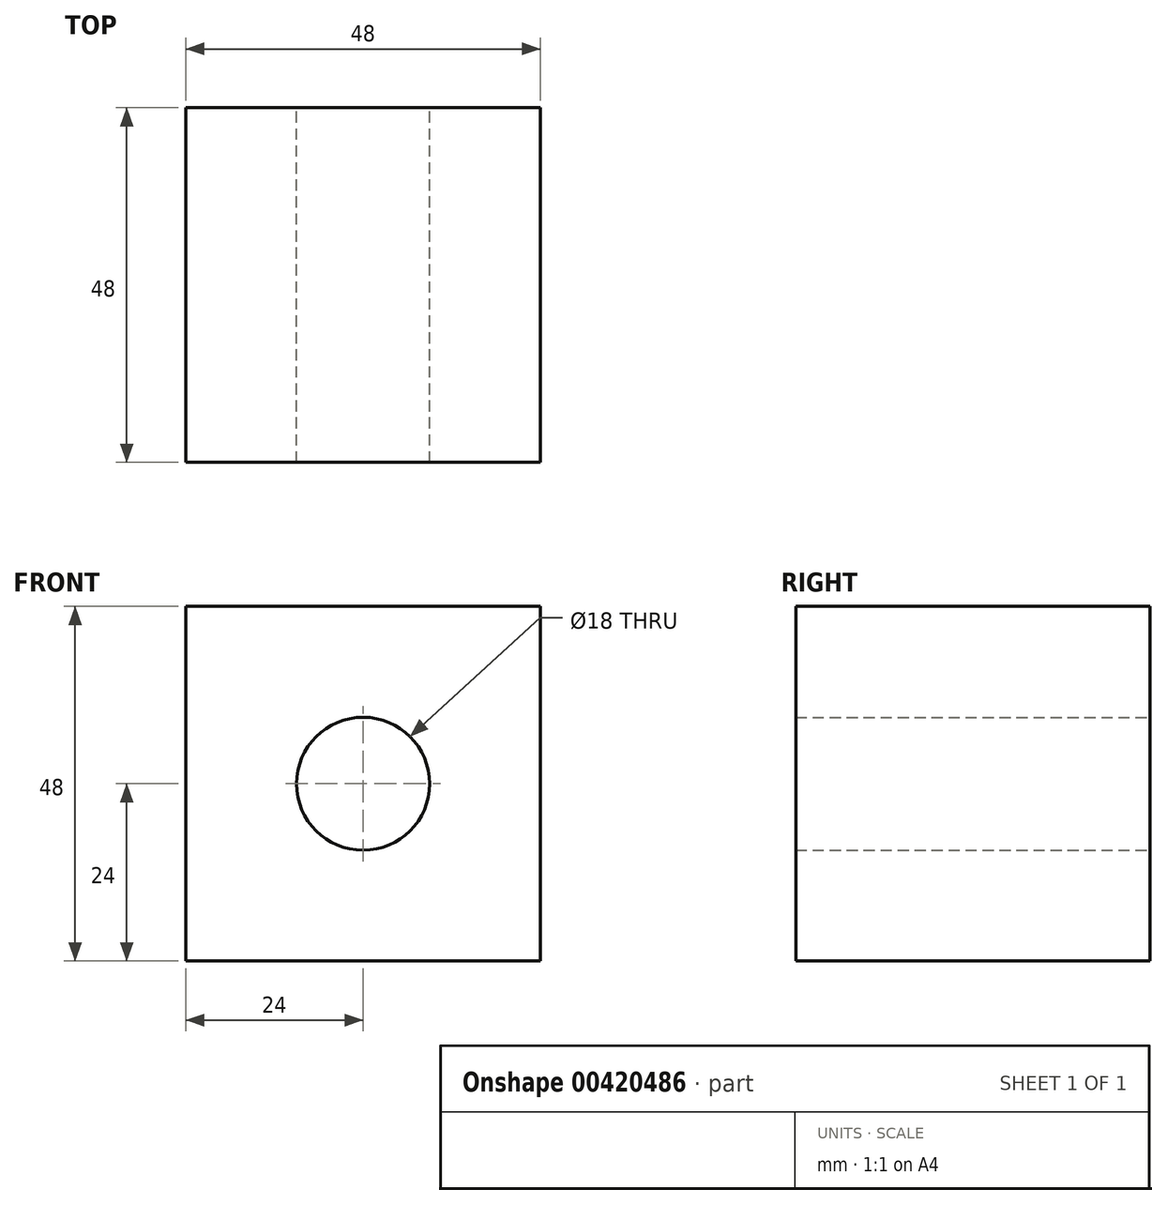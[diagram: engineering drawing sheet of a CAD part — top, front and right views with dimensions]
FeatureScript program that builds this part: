
annotation { "Feature Type Name" : "Feature", "Feature Type Description" : "" }
export const myFeature = defineFeature(function(context is Context, id is Id, definition is map)
    precondition{}
    {
        {
            var Q0;
            Q0=qCreatedBy(makeId("Front.planeOp"),FACE);
            var sketch = newSketch(context, id + "F0", { "sketchPlane" : qUnion([Q0])});
            skLineSegment(sketch, "E0.bottom", {"start": v(-24, 24) * mm, "end": v(24, 24) * mm});
            skLineSegment(sketch, "E0.top", {"start": v(-24, -24) * mm, "end": v(24, -24) * mm});
            skLineSegment(sketch, "E0.left", {"start": v(-24, 24) * mm, "end": v(-24, -24) * mm});
            skLineSegment(sketch, "E0.right", {"start": v(24, 24) * mm, "end": v(24, -24) * mm});
            skPoint(sketch, "E0.middle", {"position": v(0, 0) * mm});
            skSolve(sketch);
        }
        {
            var Q0;
            Q0=makeQuery(id+"F0.imprint","IMPRINT",FACE,{"disambiguationData":[TD([[makeQuery(id+"F0.imprint","IMPRINT",EDGE,{"derivedFrom":sQuery(id+"F0.wireOp",EDGE,"E0.bottom")}),-1.0]])]});
            extrude(context, id + "F1", {"entities" : qUnion([Q0]), "depth" : 48 * mm});
        }
        {
            var Q0;
            Q0=qCreatedBy(makeId("Front.planeOp"),FACE);
            var sketch = newSketch(context, id + "F2", { "sketchPlane" : qUnion([Q0])});
            skPoint(sketch, "E1", {"position": v(0, 0) * mm});
            skSolve(sketch);
        }
        {
            var Q0;
            Q0=sQuery(id+"F2.wireOp",VERTEX,"E1");
            var Q1;
            Q1=makeQuery(id+"F1.opExtrude","SWEPT_BODY",BODY,{"disambiguationData":[OSD([sQuery(id+"F0.wireOp",EDGE,"E0.bottom"),sQuery(id+"F0.wireOp",EDGE,"E0.top"),sQuery(id+"F0.wireOp",EDGE,"E0.left"),sQuery(id+"F0.wireOp",EDGE,"E0.right")])]});
            hole(context, id + "F3", {"style" : HoleStyle.SIMPLE, "endStyle" : HoleEndStyle.THROUGH, "oppositeDirection" : true, "holeDiameter" : 18 * mm, "isTappedThrough" : true, "tappedDepth" : 12 * mm, "tapClearance" : 3, "locations" : qUnion([Q0]), "scope" : qUnion([Q1])});
        }
    });
